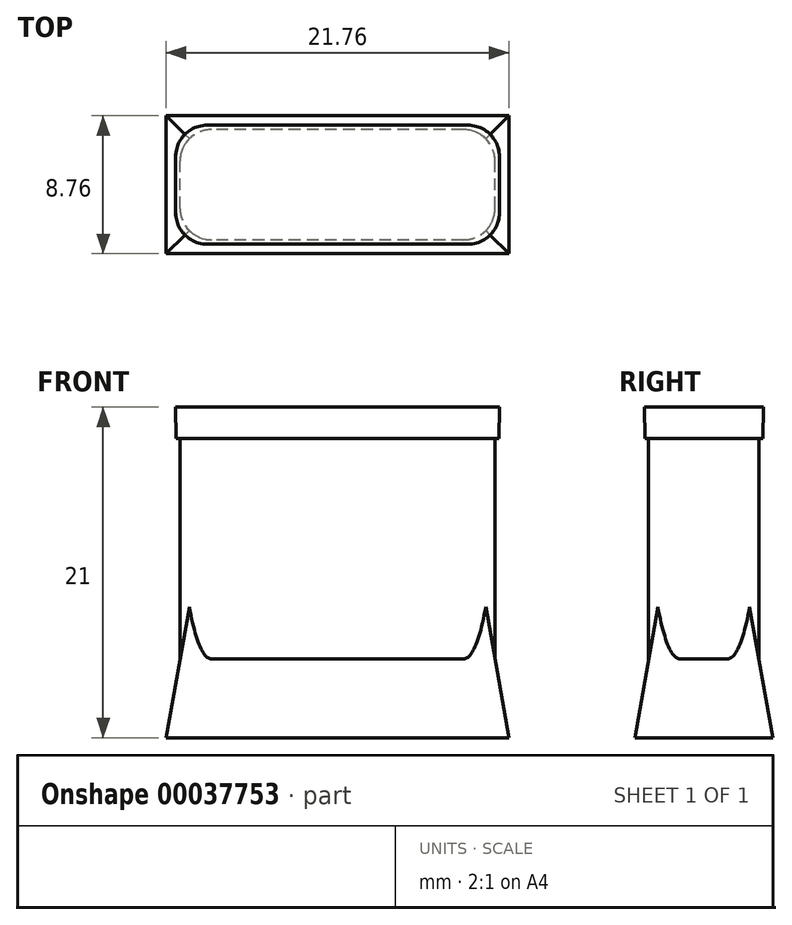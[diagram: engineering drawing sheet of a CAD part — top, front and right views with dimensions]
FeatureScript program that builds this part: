
annotation { "Feature Type Name" : "Feature", "Feature Type Description" : "" }
export const myFeature = defineFeature(function(context is Context, id is Id, definition is map)
    precondition{}
    {
        {
            var Q0;
            Q0=qCreatedBy(makeId("Top.planeOp"),FACE);
            var sketch = newSketch(context, id + "F0", { "sketchPlane" : qUnion([Q0])});
            skLineSegment(sketch, "E0.rect.bottom", {"start": v(10, -3.5) * mm, "end": v(-10, -3.5) * mm});
            skLineSegment(sketch, "E0.rect.top", {"start": v(10, 3.5) * mm, "end": v(-10, 3.5) * mm});
            skLineSegment(sketch, "E0.rect.left", {"start": v(10, -3.5) * mm, "end": v(10, 3.5) * mm});
            skLineSegment(sketch, "E0.rect.right", {"start": v(-10, -3.5) * mm, "end": v(-10, 3.5) * mm});
            skPoint(sketch, "E0.rect.middle", {"position": v(0, 0) * mm});
            skSolve(sketch);
        }
        {
            var Q0;
            Q0 = qSketchRegion(id + "F0", true);
            extrude(context, id + "F1", {"entities" : qUnion([Q0]), "depth" : 15 * mm});
        }
        {
            var Q0;
            Q0 = qSketchRegion(id + "F0", true);
            extrude(context, id + "F2", {"entities" : qUnion([Q0]), "operationType" : NewBodyOperationType.ADD, "oppositeDirection" : true, "depth" : 5 * mm, "hasDraft" : true, "draftAngle" : 10 * degree});
        }
        {
            var Q0;
            Q0 = qSketchRegion(id + "F0", true);
            extrude(context, id + "F3", {"entities" : qUnion([Q0]), "operationType" : NewBodyOperationType.ADD, "depth" : 16 * mm, "hasDraft" : true, "draftAngle" : 1 * degree, "hasSecondDirection" : true, "secondDirectionOppositeDirection" : false, "secondDirectionDepth" : 14 * mm});
        }
        {
            var Q0;
            Q0=makeQuery(id+"F1.opExtrude","SWEPT_EDGE",EDGE,{"disambiguationData":[OSD([sQuery(id+"F0.wireOp",EDGE,"E0.rect.bottom"),sQuery(id+"F0.wireOp",EDGE,"E0.rect.right")])]});
            var Q1;
            Q1=makeQuery(id+"F3.opExtrude","SWEPT_EDGE",EDGE,{"disambiguationData":[OSD([sQuery(id+"F0.wireOp",EDGE,"E0.rect.bottom"),sQuery(id+"F0.wireOp",EDGE,"E0.rect.right")])]});
            var Q2;
            Q2=makeQuery(id+"F1.opExtrude","SWEPT_EDGE",EDGE,{"disambiguationData":[OSD([sQuery(id+"F0.wireOp",EDGE,"E0.rect.top"),sQuery(id+"F0.wireOp",EDGE,"E0.rect.right")])]});
            var Q3;
            Q3=makeQuery(id+"F3.opExtrude","SWEPT_EDGE",EDGE,{"disambiguationData":[OSD([sQuery(id+"F0.wireOp",EDGE,"E0.rect.top"),sQuery(id+"F0.wireOp",EDGE,"E0.rect.right")])]});
            var Q4;
            Q4=makeQuery(id+"F1.opExtrude","SWEPT_EDGE",EDGE,{"disambiguationData":[OSD([sQuery(id+"F0.wireOp",EDGE,"E0.rect.top"),sQuery(id+"F0.wireOp",EDGE,"E0.rect.left")])]});
            var Q5;
            Q5=makeQuery(id+"F1.opExtrude","SWEPT_EDGE",EDGE,{"disambiguationData":[OSD([sQuery(id+"F0.wireOp",EDGE,"E0.rect.bottom"),sQuery(id+"F0.wireOp",EDGE,"E0.rect.left")])]});
            var Q6;
            Q6=makeQuery(id+"F3.opExtrude","SWEPT_EDGE",EDGE,{"disambiguationData":[OSD([sQuery(id+"F0.wireOp",EDGE,"E0.rect.bottom"),sQuery(id+"F0.wireOp",EDGE,"E0.rect.left")])]});
            var Q7;
            Q7=makeQuery(id+"F3.opExtrude","SWEPT_EDGE",EDGE,{"disambiguationData":[OSD([sQuery(id+"F0.wireOp",EDGE,"E0.rect.top"),sQuery(id+"F0.wireOp",EDGE,"E0.rect.left")])]});
            fillet(context, id + "F4", {"entities" : qUnion([Q0, Q1, Q2, Q3, Q4, Q5, Q6, Q7]), "radius" : 2 * mm, "tangentPropagation" : true, "allowEdgeOverflow" : false});
        }
    });
